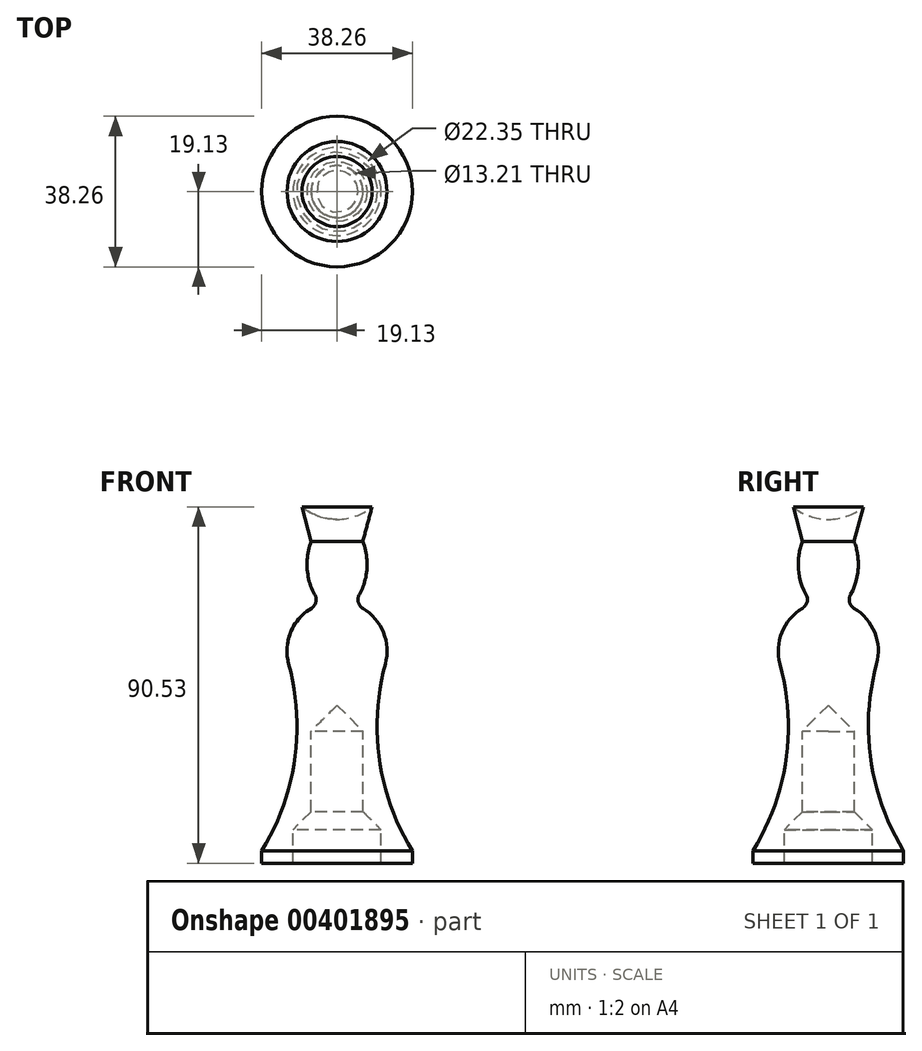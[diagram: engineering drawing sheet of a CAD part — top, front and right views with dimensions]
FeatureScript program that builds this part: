
annotation { "Feature Type Name" : "Feature", "Feature Type Description" : "" }
export const myFeature = defineFeature(function(context is Context, id is Id, definition is map)
    precondition{}
    {
        {
            var Q0;
            Q0=qCreatedBy(makeId("Front.planeOp"),FACE);
            var sketch = newSketch(context, id + "F0", { "sketchPlane" : qUnion([Q0])});
            skLineSegment(sketch, "E0", {"start": v(0, 87.35) * mm, "end": v(0, 40.13) * mm});
            skLineSegment(sketch, "E1", {"start": v(0, 0) * mm, "end": v(-11.18, 0) * mm, "construction": true});
            skLineSegment(sketch, "E2", {"start": v(-19.13, 0) * mm, "end": v(-19.13, 3.17) * mm});
            skArc(sketch, "E3", {"start": v(-19.13, 3.17) * mm, "mid": v(-10.78, 26.17) * mm, "end": v(-12.26, 50.59) * mm});
            skArc(sketch, "E4", {"start": v(-3.81, 66.02) * mm, "mid": v(-11.14, 60) * mm, "end": v(-12.26, 50.59) * mm});
            skArc(sketch, "E5", {"start": v(-8.89, 90.53) * mm, "mid": v(-4.72, 88.17) * mm, "end": v(0, 87.35) * mm});
            skLineSegment(sketch, "E6", {"start": v(-8.89, 90.53) * mm, "end": v(-6.54, 81.77) * mm});
            skEllipticalArc(sketch, "E7", {});
            skPoint(sketch, "E8", {"position": v(0, 64.5) * mm});
            skLineSegment(sketch, "E9", {"start": v(0, 40.13) * mm, "end": v(0, 40.13) * mm});
            skLineSegment(sketch, "E10", {"start": v(-6.6, 33.53) * mm, "end": v(-6.6, 13.08) * mm});
            skLineSegment(sketch, "E11", {"start": v(-6.6, 13.08) * mm, "end": v(-11.18, 8.5) * mm});
            skLineSegment(sketch, "E12", {"start": v(-11.18, 8.5) * mm, "end": v(-11.18, 0) * mm});
            skLineSegment(sketch, "E13", {"start": v(0, 40.13) * mm, "end": v(-6.6, 33.53) * mm});
            skLineSegment(sketch, "E14", {"start": v(-11.18, 0) * mm, "end": v(-19.13, 0) * mm});
            skLineSegment(sketch, "E15", {"start": v(0, 40.13) * mm, "end": v(0, 0) * mm, "construction": true});
            const initialGuessF0  = {"E7": [0, 0.07592060000000003, 0, 1, 0.01143, 0.00762, 1.0331645714438338, 2.6179938779914957]};
            skSetInitialGuess(sketch, initialGuessF0);
            skSolve(sketch);
        }
        {
            var Q0;
            Q0 = qSketchRegion(id + "F0", true);
            var Q1;
            Q1=sQuery(id+"F0.wireOp",EDGE,"E0");
            revolve(context, id + "F1", {"entities" : qUnion([Q0]), "axis" : qUnion([Q1]), "revolveType" : RevolveType.FULL});
        }
        {
            var Q0;
            Q0=makeQuery(id+"F1.opRevolve","SWEPT_EDGE",EDGE,{"disambiguationData":[OSD([sQuery(id+"F0.wireOp",EDGE,"E4"),sQuery(id+"F0.wireOp",EDGE,"E7")])]});
            fillet(context, id + "F2", {"entities" : qUnion([Q0]), "radius" : 2.54 * mm, "tangentPropagation" : true, "allowEdgeOverflow" : false});
        }
    });
